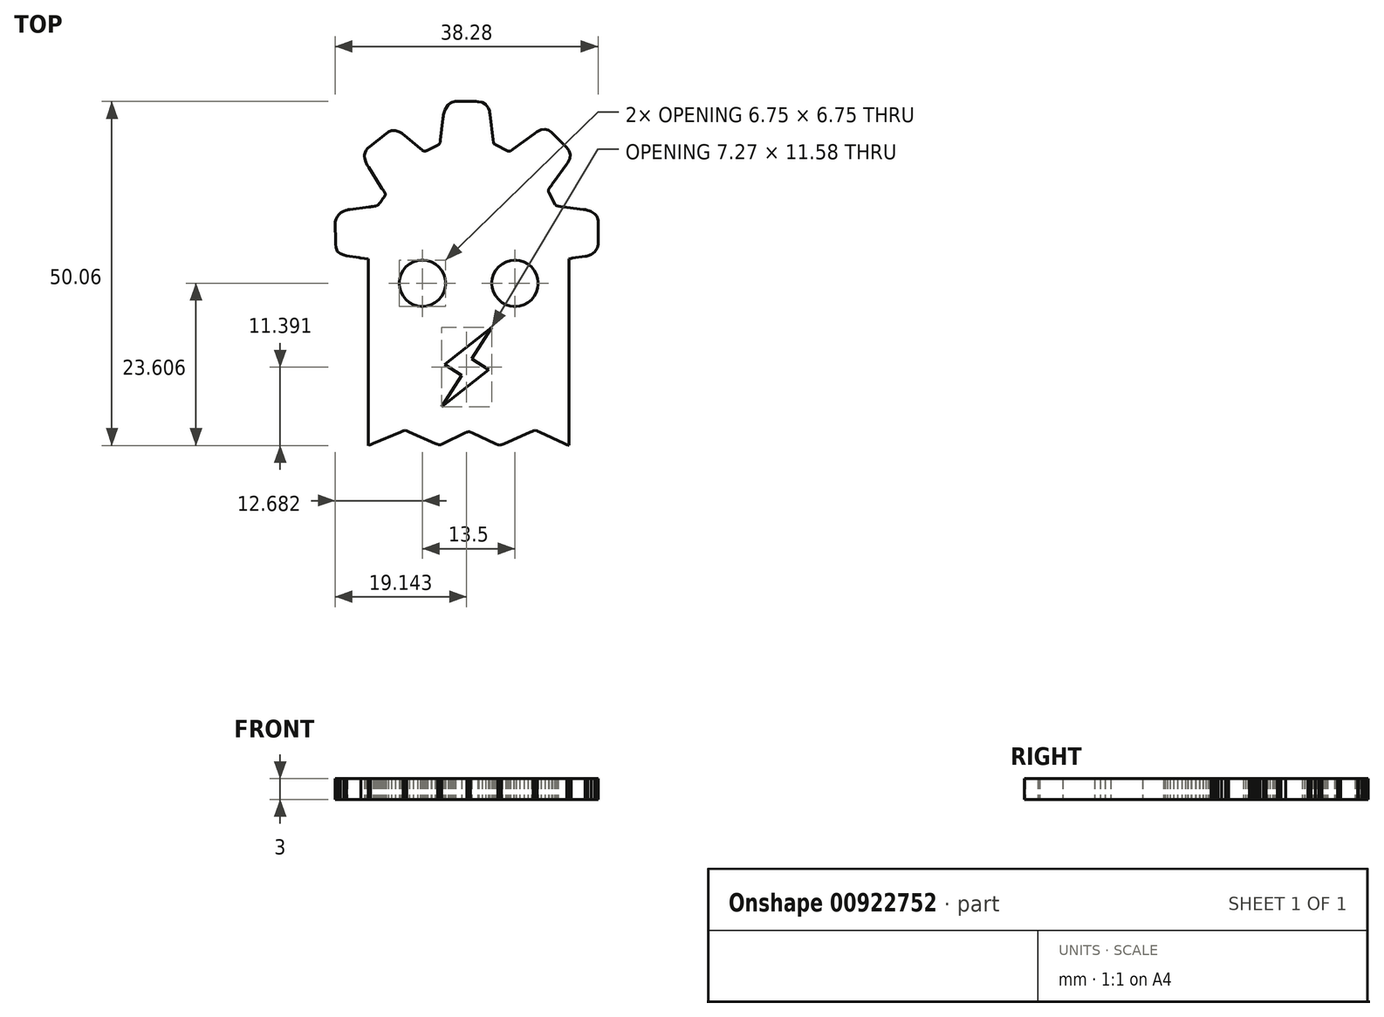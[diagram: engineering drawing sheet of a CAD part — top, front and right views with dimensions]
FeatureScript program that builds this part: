
annotation { "Feature Type Name" : "Feature", "Feature Type Description" : "" }
export const myFeature = defineFeature(function(context is Context, id is Id, definition is map)
    precondition{}
    {
        {
            var Q0;
            Q0=qCreatedBy(makeId("Top.planeOp"),FACE);
            var sketch = newSketch(context, id + "F0", { "sketchPlane" : qUnion([Q0])});
            skLineSegment(sketch, "E0", {"start": v(2.48, 0.36) * mm, "end": v(2.48, -4.17) * mm});
            skLineSegment(sketch, "E1", {"start": v(2.48, -4.17) * mm, "end": v(2.48, -4.17) * mm});
            skLineSegment(sketch, "E2", {"start": v(2.48, -4.17) * mm, "end": v(2.44, -4.15) * mm});
            skLineSegment(sketch, "E3", {"start": v(2.44, -4.15) * mm, "end": v(2.43, -4.15) * mm});
            skLineSegment(sketch, "E4", {"start": v(2.43, -4.15) * mm, "end": v(2.37, -4.12) * mm});
            skLineSegment(sketch, "E5", {"start": v(2.37, -4.12) * mm, "end": v(1.78, -3.85) * mm});
            skLineSegment(sketch, "E6", {"start": v(1.78, -3.85) * mm, "end": v(1.72, -3.82) * mm});
            skLineSegment(sketch, "E7", {"start": v(1.72, -3.82) * mm, "end": v(1.7, -3.82) * mm});
            skLineSegment(sketch, "E8", {"start": v(1.7, -3.82) * mm, "end": v(1.66, -3.8) * mm});
            skLineSegment(sketch, "E9", {"start": v(1.66, -3.8) * mm, "end": v(1.62, -3.82) * mm});
            skLineSegment(sketch, "E10", {"start": v(1.62, -3.82) * mm, "end": v(1.6, -3.82) * mm});
            skLineSegment(sketch, "E11", {"start": v(1.6, -3.82) * mm, "end": v(1.54, -3.85) * mm});
            skLineSegment(sketch, "E12", {"start": v(1.54, -3.85) * mm, "end": v(0.9, -4.13) * mm});
            skLineSegment(sketch, "E13", {"start": v(0.9, -4.13) * mm, "end": v(0.84, -4.16) * mm});
            skLineSegment(sketch, "E14", {"start": v(0.84, -4.16) * mm, "end": v(0.83, -4.16) * mm});
            skLineSegment(sketch, "E15", {"start": v(0.83, -4.16) * mm, "end": v(0.8, -4.16) * mm});
            skLineSegment(sketch, "E16", {"start": v(0.8, -4.16) * mm, "end": v(0.77, -4.16) * mm});
            skLineSegment(sketch, "E17", {"start": v(0.77, -4.16) * mm, "end": v(0.76, -4.16) * mm});
            skLineSegment(sketch, "E18", {"start": v(0.76, -4.16) * mm, "end": v(0.7, -4.13) * mm});
            skLineSegment(sketch, "E19", {"start": v(0.7, -4.13) * mm, "end": v(0.15, -3.87) * mm});
            skLineSegment(sketch, "E20", {"start": v(0.15, -3.87) * mm, "end": v(0.1, -3.85) * mm});
            skLineSegment(sketch, "E21", {"start": v(0.1, -3.85) * mm, "end": v(0.09, -3.84) * mm});
            skLineSegment(sketch, "E22", {"start": v(0.09, -3.84) * mm, "end": v(0.05, -3.84) * mm});
            skLineSegment(sketch, "E23", {"start": v(0.05, -3.84) * mm, "end": v(0.01, -3.84) * mm});
            skLineSegment(sketch, "E24", {"start": v(0.01, -3.84) * mm, "end": v(0, -3.85) * mm});
            skLineSegment(sketch, "E25", {"start": v(0, -3.85) * mm, "end": v(-0.05, -3.87) * mm});
            skLineSegment(sketch, "E26", {"start": v(-0.05, -3.87) * mm, "end": v(-0.56, -4.12) * mm});
            skLineSegment(sketch, "E27", {"start": v(-0.56, -4.12) * mm, "end": v(-0.61, -4.15) * mm});
            skLineSegment(sketch, "E28", {"start": v(-0.61, -4.15) * mm, "end": v(-0.62, -4.15) * mm});
            skLineSegment(sketch, "E29", {"start": v(-0.62, -4.15) * mm, "end": v(-0.66, -4.16) * mm});
            skLineSegment(sketch, "E30", {"start": v(-0.66, -4.16) * mm, "end": v(-0.7, -4.15) * mm});
            skLineSegment(sketch, "E31", {"start": v(-0.7, -4.15) * mm, "end": v(-0.7, -4.15) * mm});
            skLineSegment(sketch, "E32", {"start": v(-0.7, -4.15) * mm, "end": v(-0.77, -4.12) * mm});
            skLineSegment(sketch, "E33", {"start": v(-0.77, -4.12) * mm, "end": v(-1.39, -3.84) * mm});
            skLineSegment(sketch, "E34", {"start": v(-1.39, -3.84) * mm, "end": v(-1.45, -3.81) * mm});
            skLineSegment(sketch, "E35", {"start": v(-1.45, -3.81) * mm, "end": v(-1.46, -3.81) * mm});
            skLineSegment(sketch, "E36", {"start": v(-1.46, -3.81) * mm, "end": v(-1.5, -3.8) * mm});
            skLineSegment(sketch, "E37", {"start": v(-1.5, -3.8) * mm, "end": v(-1.53, -3.81) * mm});
            skLineSegment(sketch, "E38", {"start": v(-1.53, -3.81) * mm, "end": v(-1.54, -3.81) * mm});
            skLineSegment(sketch, "E39", {"start": v(-1.54, -3.81) * mm, "end": v(-1.6, -3.84) * mm});
            skLineSegment(sketch, "E40", {"start": v(-1.6, -3.84) * mm, "end": v(-2.27, -4.12) * mm});
            skLineSegment(sketch, "E41", {"start": v(-2.27, -4.12) * mm, "end": v(-2.33, -4.15) * mm});
            skLineSegment(sketch, "E42", {"start": v(-2.33, -4.15) * mm, "end": v(-2.34, -4.15) * mm});
            skLineSegment(sketch, "E43", {"start": v(-2.34, -4.15) * mm, "end": v(-2.38, -4.17) * mm});
            skLineSegment(sketch, "E44", {"start": v(-2.38, -4.17) * mm, "end": v(-2.38, -4.17) * mm});
            skLineSegment(sketch, "E45", {"start": v(-2.38, -4.17) * mm, "end": v(-2.38, 0.35) * mm});
            skLineSegment(sketch, "E46", {"start": v(-2.38, 0.35) * mm, "end": v(-2.4, 0.35) * mm});
            skLineSegment(sketch, "E47", {"start": v(-2.4, 0.35) * mm, "end": v(-2.56, 0.37) * mm});
            skLineSegment(sketch, "E48", {"start": v(-2.56, 0.37) * mm, "end": v(-2.58, 0.38) * mm});
            skLineSegment(sketch, "E49", {"start": v(-2.58, 0.38) * mm, "end": v(-2.6, 0.38) * mm});
            skLineSegment(sketch, "E50", {"start": v(-2.6, 0.38) * mm, "end": v(-2.92, 0.43) * mm});
            skLineSegment(sketch, "E51", {"start": v(-2.92, 0.43) * mm, "end": v(-2.95, 0.44) * mm});
            skLineSegment(sketch, "E52", {"start": v(-2.95, 0.44) * mm, "end": v(-2.98, 0.45) * mm});
            skLineSegment(sketch, "E53", {"start": v(-2.98, 0.45) * mm, "end": v(-3.06, 0.48) * mm});
            skLineSegment(sketch, "E54", {"start": v(-3.06, 0.48) * mm, "end": v(-3.13, 0.54) * mm});
            skLineSegment(sketch, "E55", {"start": v(-3.13, 0.54) * mm, "end": v(-3.17, 0.62) * mm});
            skLineSegment(sketch, "E56", {"start": v(-3.17, 0.62) * mm, "end": v(-3.18, 0.71) * mm});
            skLineSegment(sketch, "E57", {"start": v(-3.18, 0.71) * mm, "end": v(-3.18, 0.74) * mm});
            skLineSegment(sketch, "E58", {"start": v(-3.18, 0.74) * mm, "end": v(-3.18, 0.85) * mm});
            skLineSegment(sketch, "E59", {"start": v(-3.18, 0.85) * mm, "end": v(-3.19, 1.14) * mm});
            skLineSegment(sketch, "E60", {"start": v(-3.19, 1.14) * mm, "end": v(-3.19, 1.17) * mm});
            skLineSegment(sketch, "E61", {"start": v(-3.19, 1.17) * mm, "end": v(-3.19, 1.2) * mm});
            skLineSegment(sketch, "E62", {"start": v(-3.19, 1.2) * mm, "end": v(-3.19, 1.25) * mm});
            skLineSegment(sketch, "E63", {"start": v(-3.19, 1.25) * mm, "end": v(-3.17, 1.32) * mm});
            skLineSegment(sketch, "E64", {"start": v(-3.17, 1.32) * mm, "end": v(-3.14, 1.38) * mm});
            skLineSegment(sketch, "E65", {"start": v(-3.14, 1.38) * mm, "end": v(-3.1, 1.43) * mm});
            skLineSegment(sketch, "E66", {"start": v(-3.1, 1.43) * mm, "end": v(-3.05, 1.47) * mm});
            skLineSegment(sketch, "E67", {"start": v(-3.05, 1.47) * mm, "end": v(-3, 1.5) * mm});
            skLineSegment(sketch, "E68", {"start": v(-3, 1.5) * mm, "end": v(-2.94, 1.53) * mm});
            skLineSegment(sketch, "E69", {"start": v(-2.94, 1.53) * mm, "end": v(-2.9, 1.54) * mm});
            skLineSegment(sketch, "E70", {"start": v(-2.9, 1.54) * mm, "end": v(-2.88, 1.55) * mm});
            skLineSegment(sketch, "E71", {"start": v(-2.88, 1.55) * mm, "end": v(-2.83, 1.55) * mm});
            skLineSegment(sketch, "E72", {"start": v(-2.83, 1.55) * mm, "end": v(-2.37, 1.61) * mm});
            skLineSegment(sketch, "E73", {"start": v(-2.37, 1.61) * mm, "end": v(-2.33, 1.62) * mm});
            skLineSegment(sketch, "E74", {"start": v(-2.33, 1.62) * mm, "end": v(-2.31, 1.62) * mm});
            skLineSegment(sketch, "E75", {"start": v(-2.31, 1.62) * mm, "end": v(-2.27, 1.62) * mm});
            skLineSegment(sketch, "E76", {"start": v(-2.27, 1.62) * mm, "end": v(-2.23, 1.63) * mm});
            skLineSegment(sketch, "E77", {"start": v(-2.23, 1.63) * mm, "end": v(-2.2, 1.64) * mm});
            skLineSegment(sketch, "E78", {"start": v(-2.2, 1.64) * mm, "end": v(-2.17, 1.65) * mm});
            skLineSegment(sketch, "E79", {"start": v(-2.17, 1.65) * mm, "end": v(-2.14, 1.67) * mm});
            skLineSegment(sketch, "E80", {"start": v(-2.14, 1.67) * mm, "end": v(-2.12, 1.7) * mm});
            skLineSegment(sketch, "E81", {"start": v(-2.12, 1.7) * mm, "end": v(-2.1, 1.73) * mm});
            skLineSegment(sketch, "E82", {"start": v(-2.1, 1.73) * mm, "end": v(-2.07, 1.76) * mm});
            skLineSegment(sketch, "E83", {"start": v(-2.07, 1.76) * mm, "end": v(-2.06, 1.78) * mm});
            skLineSegment(sketch, "E84", {"start": v(-2.06, 1.78) * mm, "end": v(-2.06, 1.79) * mm});
            skLineSegment(sketch, "E85", {"start": v(-2.06, 1.79) * mm, "end": v(-2.03, 1.81) * mm});
            skLineSegment(sketch, "E86", {"start": v(-2.03, 1.81) * mm, "end": v(-2, 1.85) * mm});
            skLineSegment(sketch, "E87", {"start": v(-2, 1.85) * mm, "end": v(-1.98, 1.88) * mm});
            skLineSegment(sketch, "E88", {"start": v(-1.98, 1.88) * mm, "end": v(-1.97, 1.91) * mm});
            skLineSegment(sketch, "E89", {"start": v(-1.97, 1.91) * mm, "end": v(-1.97, 1.92) * mm});
            skLineSegment(sketch, "E90", {"start": v(-1.97, 1.92) * mm, "end": v(-1.97, 1.93) * mm});
            skLineSegment(sketch, "E91", {"start": v(-1.97, 1.93) * mm, "end": v(-1.98, 1.95) * mm});
            skLineSegment(sketch, "E92", {"start": v(-1.98, 1.95) * mm, "end": v(-2, 1.99) * mm});
            skLineSegment(sketch, "E93", {"start": v(-2, 1.99) * mm, "end": v(-2.03, 2.03) * mm});
            skLineSegment(sketch, "E94", {"start": v(-2.03, 2.03) * mm, "end": v(-2.05, 2.05) * mm});
            skLineSegment(sketch, "E95", {"start": v(-2.05, 2.05) * mm, "end": v(-2.05, 2.06) * mm});
            skLineSegment(sketch, "E96", {"start": v(-2.05, 2.06) * mm, "end": v(-2.08, 2.1) * mm});
            skLineSegment(sketch, "E97", {"start": v(-2.08, 2.1) * mm, "end": v(-2.38, 2.57) * mm});
            skLineSegment(sketch, "E98", {"start": v(-2.38, 2.57) * mm, "end": v(-2.4, 2.62) * mm});
            skLineSegment(sketch, "E99", {"start": v(-2.4, 2.62) * mm, "end": v(-2.42, 2.63) * mm});
            skLineSegment(sketch, "E100", {"start": v(-2.42, 2.63) * mm, "end": v(-2.45, 2.71) * mm});
            skLineSegment(sketch, "E101", {"start": v(-2.45, 2.71) * mm, "end": v(-2.47, 2.8) * mm});
            skLineSegment(sketch, "E102", {"start": v(-2.47, 2.8) * mm, "end": v(-2.47, 2.8) * mm});
            skLineSegment(sketch, "E103", {"start": v(-2.47, 2.8) * mm, "end": v(-2.48, 2.82) * mm});
            skLineSegment(sketch, "E104", {"start": v(-2.48, 2.82) * mm, "end": v(-2.48, 2.87) * mm});
            skLineSegment(sketch, "E105", {"start": v(-2.48, 2.87) * mm, "end": v(-2.46, 2.93) * mm});
            skLineSegment(sketch, "E106", {"start": v(-2.46, 2.93) * mm, "end": v(-2.44, 3) * mm});
            skLineSegment(sketch, "E107", {"start": v(-2.44, 3) * mm, "end": v(-2.4, 3.03) * mm});
            skLineSegment(sketch, "E108", {"start": v(-2.4, 3.03) * mm, "end": v(-2.4, 3.04) * mm});
            skLineSegment(sketch, "E109", {"start": v(-2.4, 3.04) * mm, "end": v(-2.35, 3.07) * mm});
            skLineSegment(sketch, "E110", {"start": v(-2.35, 3.07) * mm, "end": v(-1.95, 3.4) * mm});
            skLineSegment(sketch, "E111", {"start": v(-1.95, 3.4) * mm, "end": v(-1.91, 3.42) * mm});
            skLineSegment(sketch, "E112", {"start": v(-1.91, 3.42) * mm, "end": v(-1.9, 3.43) * mm});
            skLineSegment(sketch, "E113", {"start": v(-1.9, 3.43) * mm, "end": v(-1.83, 3.46) * mm});
            skLineSegment(sketch, "E114", {"start": v(-1.83, 3.46) * mm, "end": v(-1.73, 3.47) * mm});
            skLineSegment(sketch, "E115", {"start": v(-1.73, 3.47) * mm, "end": v(-1.64, 3.44) * mm});
            skLineSegment(sketch, "E116", {"start": v(-1.64, 3.44) * mm, "end": v(-1.57, 3.4) * mm});
            skLineSegment(sketch, "E117", {"start": v(-1.57, 3.4) * mm, "end": v(-1.55, 3.38) * mm});
            skLineSegment(sketch, "E118", {"start": v(-1.55, 3.38) * mm, "end": v(-1.5, 3.35) * mm});
            skLineSegment(sketch, "E119", {"start": v(-1.5, 3.35) * mm, "end": v(-1.12, 3.03) * mm});
            skLineSegment(sketch, "E120", {"start": v(-1.12, 3.03) * mm, "end": v(-1.09, 3) * mm});
            skLineSegment(sketch, "E121", {"start": v(-1.09, 3) * mm, "end": v(-1.08, 2.99) * mm});
            skLineSegment(sketch, "E122", {"start": v(-1.08, 2.99) * mm, "end": v(-1.06, 2.97) * mm});
            skLineSegment(sketch, "E123", {"start": v(-1.06, 2.97) * mm, "end": v(-1.03, 2.97) * mm});
            skLineSegment(sketch, "E124", {"start": v(-1.03, 2.97) * mm, "end": v(-1, 2.97) * mm});
            skLineSegment(sketch, "E125", {"start": v(-1, 2.97) * mm, "end": v(-0.98, 2.98) * mm});
            skLineSegment(sketch, "E126", {"start": v(-0.98, 2.98) * mm, "end": v(-0.97, 2.98) * mm});
            skLineSegment(sketch, "E127", {"start": v(-0.97, 2.98) * mm, "end": v(-0.95, 3) * mm});
            skLineSegment(sketch, "E128", {"start": v(-0.95, 3) * mm, "end": v(-0.71, 3.1) * mm});
            skLineSegment(sketch, "E129", {"start": v(-0.71, 3.1) * mm, "end": v(-0.69, 3.12) * mm});
            skLineSegment(sketch, "E130", {"start": v(-0.69, 3.12) * mm, "end": v(-0.68, 3.12) * mm});
            skLineSegment(sketch, "E131", {"start": v(-0.68, 3.12) * mm, "end": v(-0.66, 3.14) * mm});
            skLineSegment(sketch, "E132", {"start": v(-0.66, 3.14) * mm, "end": v(-0.64, 3.18) * mm});
            skLineSegment(sketch, "E133", {"start": v(-0.64, 3.18) * mm, "end": v(-0.64, 3.18) * mm});
            skLineSegment(sketch, "E134", {"start": v(-0.64, 3.18) * mm, "end": v(-0.64, 3.24) * mm});
            skLineSegment(sketch, "E135", {"start": v(-0.64, 3.24) * mm, "end": v(-0.57, 3.77) * mm});
            skLineSegment(sketch, "E136", {"start": v(-0.57, 3.77) * mm, "end": v(-0.57, 3.82) * mm});
            skLineSegment(sketch, "E137", {"start": v(-0.57, 3.82) * mm, "end": v(-0.56, 3.85) * mm});
            skLineSegment(sketch, "E138", {"start": v(-0.56, 3.85) * mm, "end": v(-0.52, 3.98) * mm});
            skLineSegment(sketch, "E139", {"start": v(-0.52, 3.98) * mm, "end": v(-0.44, 4.09) * mm});
            skLineSegment(sketch, "E140", {"start": v(-0.44, 4.09) * mm, "end": v(-0.42, 4.1) * mm});
            skLineSegment(sketch, "E141", {"start": v(-0.42, 4.1) * mm, "end": v(-0.42, 4.11) * mm});
            skLineSegment(sketch, "E142", {"start": v(-0.42, 4.11) * mm, "end": v(-0.4, 4.14) * mm});
            skLineSegment(sketch, "E143", {"start": v(-0.4, 4.14) * mm, "end": v(-0.35, 4.16) * mm});
            skLineSegment(sketch, "E144", {"start": v(-0.35, 4.16) * mm, "end": v(-0.31, 4.17) * mm});
            skLineSegment(sketch, "E145", {"start": v(-0.31, 4.17) * mm, "end": v(-0.28, 4.17) * mm});
            skLineSegment(sketch, "E146", {"start": v(-0.28, 4.17) * mm, "end": v(-0.27, 4.17) * mm});
            skLineSegment(sketch, "E147", {"start": v(-0.27, 4.17) * mm, "end": v(-0.22, 4.17) * mm});
            skLineSegment(sketch, "E148", {"start": v(-0.22, 4.17) * mm, "end": v(0.23, 4.17) * mm});
            skLineSegment(sketch, "E149", {"start": v(0.23, 4.17) * mm, "end": v(0.27, 4.17) * mm});
            skLineSegment(sketch, "E150", {"start": v(0.27, 4.17) * mm, "end": v(0.3, 4.17) * mm});
            skLineSegment(sketch, "E151", {"start": v(0.3, 4.17) * mm, "end": v(0.38, 4.15) * mm});
            skLineSegment(sketch, "E152", {"start": v(0.38, 4.15) * mm, "end": v(0.46, 4.1) * mm});
            skLineSegment(sketch, "E153", {"start": v(0.46, 4.1) * mm, "end": v(0.53, 4.02) * mm});
            skLineSegment(sketch, "E154", {"start": v(0.53, 4.02) * mm, "end": v(0.56, 3.94) * mm});
            skLineSegment(sketch, "E155", {"start": v(0.56, 3.94) * mm, "end": v(0.56, 3.91) * mm});
            skLineSegment(sketch, "E156", {"start": v(0.56, 3.91) * mm, "end": v(0.57, 3.85) * mm});
            skLineSegment(sketch, "E157", {"start": v(0.57, 3.85) * mm, "end": v(0.65, 3.24) * mm});
            skLineSegment(sketch, "E158", {"start": v(0.65, 3.24) * mm, "end": v(0.65, 3.18) * mm});
            skLineSegment(sketch, "E159", {"start": v(0.65, 3.18) * mm, "end": v(0.65, 3.18) * mm});
            skLineSegment(sketch, "E160", {"start": v(0.65, 3.18) * mm, "end": v(0.67, 3.15) * mm});
            skLineSegment(sketch, "E161", {"start": v(0.67, 3.15) * mm, "end": v(0.69, 3.13) * mm});
            skLineSegment(sketch, "E162", {"start": v(0.69, 3.13) * mm, "end": v(0.7, 3.13) * mm});
            skLineSegment(sketch, "E163", {"start": v(0.7, 3.13) * mm, "end": v(0.72, 3.11) * mm});
            skLineSegment(sketch, "E164", {"start": v(0.72, 3.11) * mm, "end": v(0.97, 2.98) * mm});
            skLineSegment(sketch, "E165", {"start": v(0.97, 2.98) * mm, "end": v(1, 2.97) * mm});
            skLineSegment(sketch, "E166", {"start": v(1, 2.97) * mm, "end": v(1, 2.97) * mm});
            skLineSegment(sketch, "E167", {"start": v(1, 2.97) * mm, "end": v(1.03, 2.96) * mm});
            skLineSegment(sketch, "E168", {"start": v(1.03, 2.96) * mm, "end": v(1.06, 2.97) * mm});
            skLineSegment(sketch, "E169", {"start": v(1.06, 2.97) * mm, "end": v(1.06, 2.97) * mm});
            skLineSegment(sketch, "E170", {"start": v(1.06, 2.97) * mm, "end": v(1.11, 3.01) * mm});
            skLineSegment(sketch, "E171", {"start": v(1.11, 3.01) * mm, "end": v(1.65, 3.4) * mm});
            skLineSegment(sketch, "E172", {"start": v(1.65, 3.4) * mm, "end": v(1.7, 3.43) * mm});
            skLineSegment(sketch, "E173", {"start": v(1.7, 3.43) * mm, "end": v(1.73, 3.45) * mm});
            skLineSegment(sketch, "E174", {"start": v(1.73, 3.45) * mm, "end": v(1.8, 3.49) * mm});
            skLineSegment(sketch, "E175", {"start": v(1.8, 3.49) * mm, "end": v(1.9, 3.5) * mm});
            skLineSegment(sketch, "E176", {"start": v(1.9, 3.5) * mm, "end": v(1.99, 3.47) * mm});
            skLineSegment(sketch, "E177", {"start": v(1.99, 3.47) * mm, "end": v(2.06, 3.43) * mm});
            skLineSegment(sketch, "E178", {"start": v(2.06, 3.43) * mm, "end": v(2.08, 3.4) * mm});
            skLineSegment(sketch, "E179", {"start": v(2.08, 3.4) * mm, "end": v(2.1, 3.38) * mm});
            skLineSegment(sketch, "E180", {"start": v(2.1, 3.38) * mm, "end": v(2.39, 3.1) * mm});
            skLineSegment(sketch, "E181", {"start": v(2.39, 3.1) * mm, "end": v(2.42, 3.07) * mm});
            skLineSegment(sketch, "E182", {"start": v(2.42, 3.07) * mm, "end": v(2.44, 3.05) * mm});
            skLineSegment(sketch, "E183", {"start": v(2.44, 3.05) * mm, "end": v(2.49, 2.98) * mm});
            skLineSegment(sketch, "E184", {"start": v(2.49, 2.98) * mm, "end": v(2.52, 2.88) * mm});
            skLineSegment(sketch, "E185", {"start": v(2.52, 2.88) * mm, "end": v(2.5, 2.78) * mm});
            skLineSegment(sketch, "E186", {"start": v(2.5, 2.78) * mm, "end": v(2.47, 2.7) * mm});
            skLineSegment(sketch, "E187", {"start": v(2.47, 2.7) * mm, "end": v(2.45, 2.68) * mm});
            skLineSegment(sketch, "E188", {"start": v(2.45, 2.68) * mm, "end": v(2.42, 2.64) * mm});
            skLineSegment(sketch, "E189", {"start": v(2.42, 2.64) * mm, "end": v(2.12, 2.22) * mm});
            skLineSegment(sketch, "E190", {"start": v(2.12, 2.22) * mm, "end": v(2.09, 2.18) * mm});
            skLineSegment(sketch, "E191", {"start": v(2.09, 2.18) * mm, "end": v(2.08, 2.17) * mm});
            skLineSegment(sketch, "E192", {"start": v(2.08, 2.17) * mm, "end": v(2, 2.05) * mm});
            skLineSegment(sketch, "E193", {"start": v(2, 2.05) * mm, "end": v(2, 2.04) * mm});
            skLineSegment(sketch, "E194", {"start": v(2, 2.04) * mm, "end": v(1.99, 2.04) * mm});
            skLineSegment(sketch, "E195", {"start": v(1.99, 2.04) * mm, "end": v(1.98, 2.02) * mm});
            skLineSegment(sketch, "E196", {"start": v(1.98, 2.02) * mm, "end": v(1.99, 2) * mm});
            skLineSegment(sketch, "E197", {"start": v(1.99, 2) * mm, "end": v(1.99, 1.99) * mm});
            skLineSegment(sketch, "E198", {"start": v(1.99, 1.99) * mm, "end": v(2, 1.96) * mm});
            skLineSegment(sketch, "E199", {"start": v(2, 1.96) * mm, "end": v(2.13, 1.7) * mm});
            skLineSegment(sketch, "E200", {"start": v(2.13, 1.7) * mm, "end": v(2.15, 1.67) * mm});
            skLineSegment(sketch, "E201", {"start": v(2.15, 1.67) * mm, "end": v(2.15, 1.66) * mm});
            skLineSegment(sketch, "E202", {"start": v(2.15, 1.66) * mm, "end": v(2.18, 1.64) * mm});
            skLineSegment(sketch, "E203", {"start": v(2.18, 1.64) * mm, "end": v(2.21, 1.63) * mm});
            skLineSegment(sketch, "E204", {"start": v(2.21, 1.63) * mm, "end": v(2.22, 1.63) * mm});
            skLineSegment(sketch, "E205", {"start": v(2.22, 1.63) * mm, "end": v(2.28, 1.62) * mm});
            skLineSegment(sketch, "E206", {"start": v(2.28, 1.62) * mm, "end": v(2.83, 1.55) * mm});
            skLineSegment(sketch, "E207", {"start": v(2.83, 1.55) * mm, "end": v(2.89, 1.55) * mm});
            skLineSegment(sketch, "E208", {"start": v(2.89, 1.55) * mm, "end": v(2.9, 1.54) * mm});
            skLineSegment(sketch, "E209", {"start": v(2.9, 1.54) * mm, "end": v(3.01, 1.5) * mm});
            skLineSegment(sketch, "E210", {"start": v(3.01, 1.5) * mm, "end": v(3.1, 1.44) * mm});
            skLineSegment(sketch, "E211", {"start": v(3.1, 1.44) * mm, "end": v(3.12, 1.43) * mm});
            skLineSegment(sketch, "E212", {"start": v(3.12, 1.43) * mm, "end": v(3.13, 1.42) * mm});
            skLineSegment(sketch, "E213", {"start": v(3.13, 1.42) * mm, "end": v(3.15, 1.4) * mm});
            skLineSegment(sketch, "E214", {"start": v(3.15, 1.4) * mm, "end": v(3.17, 1.36) * mm});
            skLineSegment(sketch, "E215", {"start": v(3.17, 1.36) * mm, "end": v(3.18, 1.32) * mm});
            skLineSegment(sketch, "E216", {"start": v(3.18, 1.32) * mm, "end": v(3.19, 1.29) * mm});
            skLineSegment(sketch, "E217", {"start": v(3.19, 1.29) * mm, "end": v(3.19, 1.28) * mm});
            skLineSegment(sketch, "E218", {"start": v(3.19, 1.28) * mm, "end": v(3.19, 1.23) * mm});
            skLineSegment(sketch, "E219", {"start": v(3.19, 1.23) * mm, "end": v(3.19, 0.78) * mm});
            skLineSegment(sketch, "E220", {"start": v(3.19, 0.78) * mm, "end": v(3.19, 0.73) * mm});
            skLineSegment(sketch, "E221", {"start": v(3.19, 0.73) * mm, "end": v(3.19, 0.7) * mm});
            skLineSegment(sketch, "E222", {"start": v(3.19, 0.7) * mm, "end": v(3.17, 0.61) * mm});
            skLineSegment(sketch, "E223", {"start": v(3.17, 0.61) * mm, "end": v(3.11, 0.52) * mm});
            skLineSegment(sketch, "E224", {"start": v(3.11, 0.52) * mm, "end": v(3.02, 0.46) * mm});
            skLineSegment(sketch, "E225", {"start": v(3.02, 0.46) * mm, "end": v(2.94, 0.42) * mm});
            skLineSegment(sketch, "E226", {"start": v(2.94, 0.42) * mm, "end": v(2.9, 0.42) * mm});
            skLineSegment(sketch, "E227", {"start": v(2.9, 0.42) * mm, "end": v(2.88, 0.41) * mm});
            skLineSegment(sketch, "E228", {"start": v(2.88, 0.41) * mm, "end": v(2.57, 0.37) * mm});
            skLineSegment(sketch, "E229", {"start": v(2.57, 0.37) * mm, "end": v(2.54, 0.37) * mm});
            skLineSegment(sketch, "E230", {"start": v(2.54, 0.37) * mm, "end": v(2.53, 0.37) * mm});
            skLineSegment(sketch, "E231", {"start": v(2.53, 0.37) * mm, "end": v(2.49, 0.36) * mm});
            skLineSegment(sketch, "E232", {"start": v(2.49, 0.36) * mm, "end": v(2.48, 0.36) * mm});
            skLineSegment(sketch, "E233", {"start": v(0.6, -1.3) * mm, "end": v(0.6, -1.3) * mm});
            skLineSegment(sketch, "E234", {"start": v(0.6, -1.3) * mm, "end": v(-0.54, -2.21) * mm});
            skLineSegment(sketch, "E235", {"start": v(-0.54, -2.21) * mm, "end": v(-0.12, -2.47) * mm});
            skLineSegment(sketch, "E236", {"start": v(-0.12, -2.47) * mm, "end": v(-0.6, -3.24) * mm});
            skLineSegment(sketch, "E237", {"start": v(-0.6, -3.24) * mm, "end": v(-0.6, -3.24) * mm});
            skLineSegment(sketch, "E238", {"start": v(-0.6, -3.24) * mm, "end": v(0.54, -2.33) * mm});
            skLineSegment(sketch, "E239", {"start": v(0.54, -2.33) * mm, "end": v(0.13, -2.07) * mm});
            skLineSegment(sketch, "E240", {"start": v(0.13, -2.07) * mm, "end": v(0.6, -1.3) * mm});
            skLineSegment(sketch, "E241", {"start": v(-1.07, 0.33) * mm, "end": v(-1.1, 0.33) * mm});
            skLineSegment(sketch, "E242", {"start": v(-1.1, 0.33) * mm, "end": v(-1.19, 0.31) * mm});
            skLineSegment(sketch, "E243", {"start": v(-1.19, 0.31) * mm, "end": v(-1.3, 0.28) * mm});
            skLineSegment(sketch, "E244", {"start": v(-1.3, 0.28) * mm, "end": v(-1.39, 0.23) * mm});
            skLineSegment(sketch, "E245", {"start": v(-1.39, 0.23) * mm, "end": v(-1.47, 0.16) * mm});
            skLineSegment(sketch, "E246", {"start": v(-1.47, 0.16) * mm, "end": v(-1.54, 0.08) * mm});
            skLineSegment(sketch, "E247", {"start": v(-1.54, 0.08) * mm, "end": v(-1.6, -0.02) * mm});
            skLineSegment(sketch, "E248", {"start": v(-1.6, -0.02) * mm, "end": v(-1.63, -0.12) * mm});
            skLineSegment(sketch, "E249", {"start": v(-1.63, -0.12) * mm, "end": v(-1.64, -0.2) * mm});
            skLineSegment(sketch, "E250", {"start": v(-1.64, -0.2) * mm, "end": v(-1.64, -0.24) * mm});
            skLineSegment(sketch, "E251", {"start": v(-1.64, -0.24) * mm, "end": v(-1.64, -0.26) * mm});
            skLineSegment(sketch, "E252", {"start": v(-1.64, -0.26) * mm, "end": v(-1.63, -0.35) * mm});
            skLineSegment(sketch, "E253", {"start": v(-1.63, -0.35) * mm, "end": v(-1.6, -0.45) * mm});
            skLineSegment(sketch, "E254", {"start": v(-1.6, -0.45) * mm, "end": v(-1.54, -0.55) * mm});
            skLineSegment(sketch, "E255", {"start": v(-1.54, -0.55) * mm, "end": v(-1.48, -0.63) * mm});
            skLineSegment(sketch, "E256", {"start": v(-1.48, -0.63) * mm, "end": v(-1.4, -0.7) * mm});
            skLineSegment(sketch, "E257", {"start": v(-1.4, -0.7) * mm, "end": v(-1.3, -0.75) * mm});
            skLineSegment(sketch, "E258", {"start": v(-1.3, -0.75) * mm, "end": v(-1.2, -0.79) * mm});
            skLineSegment(sketch, "E259", {"start": v(-1.2, -0.79) * mm, "end": v(-1.1, -0.8) * mm});
            skLineSegment(sketch, "E260", {"start": v(-1.1, -0.8) * mm, "end": v(-1.08, -0.8) * mm});
            skLineSegment(sketch, "E261", {"start": v(-1.08, -0.8) * mm, "end": v(-1.05, -0.8) * mm});
            skLineSegment(sketch, "E262", {"start": v(-1.05, -0.8) * mm, "end": v(-0.97, -0.79) * mm});
            skLineSegment(sketch, "E263", {"start": v(-0.97, -0.79) * mm, "end": v(-0.86, -0.76) * mm});
            skLineSegment(sketch, "E264", {"start": v(-0.86, -0.76) * mm, "end": v(-0.76, -0.7) * mm});
            skLineSegment(sketch, "E265", {"start": v(-0.76, -0.7) * mm, "end": v(-0.68, -0.64) * mm});
            skLineSegment(sketch, "E266", {"start": v(-0.68, -0.64) * mm, "end": v(-0.61, -0.55) * mm});
            skLineSegment(sketch, "E267", {"start": v(-0.61, -0.55) * mm, "end": v(-0.56, -0.46) * mm});
            skLineSegment(sketch, "E268", {"start": v(-0.56, -0.46) * mm, "end": v(-0.53, -0.35) * mm});
            skLineSegment(sketch, "E269", {"start": v(-0.53, -0.35) * mm, "end": v(-0.51, -0.27) * mm});
            skLineSegment(sketch, "E270", {"start": v(-0.51, -0.27) * mm, "end": v(-0.51, -0.24) * mm});
            skLineSegment(sketch, "E271", {"start": v(-0.51, -0.24) * mm, "end": v(-0.51, -0.21) * mm});
            skLineSegment(sketch, "E272", {"start": v(-0.51, -0.21) * mm, "end": v(-0.52, -0.13) * mm});
            skLineSegment(sketch, "E273", {"start": v(-0.52, -0.13) * mm, "end": v(-0.56, -0.02) * mm});
            skLineSegment(sketch, "E274", {"start": v(-0.56, -0.02) * mm, "end": v(-0.6, 0.08) * mm});
            skLineSegment(sketch, "E275", {"start": v(-0.6, 0.08) * mm, "end": v(-0.68, 0.16) * mm});
            skLineSegment(sketch, "E276", {"start": v(-0.68, 0.16) * mm, "end": v(-0.76, 0.23) * mm});
            skLineSegment(sketch, "E277", {"start": v(-0.76, 0.23) * mm, "end": v(-0.86, 0.28) * mm});
            skLineSegment(sketch, "E278", {"start": v(-0.86, 0.28) * mm, "end": v(-0.96, 0.31) * mm});
            skLineSegment(sketch, "E279", {"start": v(-0.96, 0.31) * mm, "end": v(-1.05, 0.32) * mm});
            skLineSegment(sketch, "E280", {"start": v(-1.05, 0.32) * mm, "end": v(-1.07, 0.33) * mm});
            skLineSegment(sketch, "E281", {"start": v(1.18, 0.33) * mm, "end": v(1.15, 0.33) * mm});
            skLineSegment(sketch, "E282", {"start": v(1.15, 0.33) * mm, "end": v(1.06, 0.31) * mm});
            skLineSegment(sketch, "E283", {"start": v(1.06, 0.31) * mm, "end": v(0.96, 0.28) * mm});
            skLineSegment(sketch, "E284", {"start": v(0.96, 0.28) * mm, "end": v(0.86, 0.23) * mm});
            skLineSegment(sketch, "E285", {"start": v(0.86, 0.23) * mm, "end": v(0.78, 0.16) * mm});
            skLineSegment(sketch, "E286", {"start": v(0.78, 0.16) * mm, "end": v(0.7, 0.08) * mm});
            skLineSegment(sketch, "E287", {"start": v(0.7, 0.08) * mm, "end": v(0.66, -0.02) * mm});
            skLineSegment(sketch, "E288", {"start": v(0.66, -0.02) * mm, "end": v(0.62, -0.12) * mm});
            skLineSegment(sketch, "E289", {"start": v(0.62, -0.12) * mm, "end": v(0.61, -0.2) * mm});
            skLineSegment(sketch, "E290", {"start": v(0.61, -0.2) * mm, "end": v(0.61, -0.24) * mm});
            skLineSegment(sketch, "E291", {"start": v(0.61, -0.24) * mm, "end": v(0.61, -0.26) * mm});
            skLineSegment(sketch, "E292", {"start": v(0.61, -0.26) * mm, "end": v(0.62, -0.35) * mm});
            skLineSegment(sketch, "E293", {"start": v(0.62, -0.35) * mm, "end": v(0.65, -0.45) * mm});
            skLineSegment(sketch, "E294", {"start": v(0.65, -0.45) * mm, "end": v(0.7, -0.55) * mm});
            skLineSegment(sketch, "E295", {"start": v(0.7, -0.55) * mm, "end": v(0.77, -0.63) * mm});
            skLineSegment(sketch, "E296", {"start": v(0.77, -0.63) * mm, "end": v(0.86, -0.7) * mm});
            skLineSegment(sketch, "E297", {"start": v(0.86, -0.7) * mm, "end": v(0.95, -0.75) * mm});
            skLineSegment(sketch, "E298", {"start": v(0.95, -0.75) * mm, "end": v(1.06, -0.79) * mm});
            skLineSegment(sketch, "E299", {"start": v(1.06, -0.79) * mm, "end": v(1.14, -0.8) * mm});
            skLineSegment(sketch, "E300", {"start": v(1.14, -0.8) * mm, "end": v(1.17, -0.8) * mm});
            skLineSegment(sketch, "E301", {"start": v(1.17, -0.8) * mm, "end": v(1.2, -0.8) * mm});
            skLineSegment(sketch, "E302", {"start": v(1.2, -0.8) * mm, "end": v(1.28, -0.79) * mm});
            skLineSegment(sketch, "E303", {"start": v(1.28, -0.79) * mm, "end": v(1.4, -0.76) * mm});
            skLineSegment(sketch, "E304", {"start": v(1.4, -0.76) * mm, "end": v(1.49, -0.7) * mm});
            skLineSegment(sketch, "E305", {"start": v(1.49, -0.7) * mm, "end": v(1.57, -0.64) * mm});
            skLineSegment(sketch, "E306", {"start": v(1.57, -0.64) * mm, "end": v(1.64, -0.55) * mm});
            skLineSegment(sketch, "E307", {"start": v(1.64, -0.55) * mm, "end": v(1.7, -0.46) * mm});
            skLineSegment(sketch, "E308", {"start": v(1.7, -0.46) * mm, "end": v(1.72, -0.35) * mm});
            skLineSegment(sketch, "E309", {"start": v(1.72, -0.35) * mm, "end": v(1.74, -0.27) * mm});
            skLineSegment(sketch, "E310", {"start": v(1.74, -0.27) * mm, "end": v(1.74, -0.24) * mm});
            skLineSegment(sketch, "E311", {"start": v(1.74, -0.24) * mm, "end": v(1.74, -0.21) * mm});
            skLineSegment(sketch, "E312", {"start": v(1.74, -0.21) * mm, "end": v(1.73, -0.13) * mm});
            skLineSegment(sketch, "E313", {"start": v(1.73, -0.13) * mm, "end": v(1.7, -0.02) * mm});
            skLineSegment(sketch, "E314", {"start": v(1.7, -0.02) * mm, "end": v(1.64, 0.08) * mm});
            skLineSegment(sketch, "E315", {"start": v(1.64, 0.08) * mm, "end": v(1.57, 0.16) * mm});
            skLineSegment(sketch, "E316", {"start": v(1.57, 0.16) * mm, "end": v(1.49, 0.23) * mm});
            skLineSegment(sketch, "E317", {"start": v(1.49, 0.23) * mm, "end": v(1.4, 0.28) * mm});
            skLineSegment(sketch, "E318", {"start": v(1.4, 0.28) * mm, "end": v(1.29, 0.31) * mm});
            skLineSegment(sketch, "E319", {"start": v(1.29, 0.31) * mm, "end": v(1.2, 0.32) * mm});
            skLineSegment(sketch, "E320", {"start": v(1.2, 0.32) * mm, "end": v(1.18, 0.33) * mm});
            skLineSegment(sketch, "E321", {"start": v(1.18, 0.33) * mm, "end": v(1.18, 0.33) * mm});
            skSolve(sketch);
        }
        {
            var Q0;
            Q0=makeQuery(id+"F0.imprint","IMPRINT",FACE,{"disambiguationData":[TD([[makeQuery(id+"F0.imprint","IMPRINT",EDGE,{"derivedFrom":sQuery(id+"F0.wireOp",EDGE,"E0")}),-1.0]])]});
            extrude(context, id + "F1", {"entities" : qUnion([Q0]), "depth" : .25 * mm, "offsetDistance" : 25 * mm});
        }
        {
            var Q0;
            Q0=makeQuery(id+"F1.opExtrude","SWEPT_BODY",BODY,{"disambiguationData":[OSD([sQuery(id+"F0.wireOp",EDGE,"E0"),sQuery(id+"F0.wireOp",EDGE,"E1"),sQuery(id+"F0.wireOp",EDGE,"E2"),sQuery(id+"F0.wireOp",EDGE,"E3"),sQuery(id+"F0.wireOp",EDGE,"E4"),sQuery(id+"F0.wireOp",EDGE,"E5"),sQuery(id+"F0.wireOp",EDGE,"E6"),sQuery(id+"F0.wireOp",EDGE,"E7"),sQuery(id+"F0.wireOp",EDGE,"E8"),sQuery(id+"F0.wireOp",EDGE,"E9"),sQuery(id+"F0.wireOp",EDGE,"E10"),sQuery(id+"F0.wireOp",EDGE,"E11"),sQuery(id+"F0.wireOp",EDGE,"E12"),sQuery(id+"F0.wireOp",EDGE,"E13"),sQuery(id+"F0.wireOp",EDGE,"E14"),sQuery(id+"F0.wireOp",EDGE,"E15"),sQuery(id+"F0.wireOp",EDGE,"E16"),sQuery(id+"F0.wireOp",EDGE,"E17"),sQuery(id+"F0.wireOp",EDGE,"E18"),sQuery(id+"F0.wireOp",EDGE,"E19"),sQuery(id+"F0.wireOp",EDGE,"E20"),sQuery(id+"F0.wireOp",EDGE,"E21"),sQuery(id+"F0.wireOp",EDGE,"E22"),sQuery(id+"F0.wireOp",EDGE,"E23"),sQuery(id+"F0.wireOp",EDGE,"E24"),sQuery(id+"F0.wireOp",EDGE,"E25"),sQuery(id+"F0.wireOp",EDGE,"E26"),sQuery(id+"F0.wireOp",EDGE,"E27"),sQuery(id+"F0.wireOp",EDGE,"E28"),sQuery(id+"F0.wireOp",EDGE,"E29"),sQuery(id+"F0.wireOp",EDGE,"E30"),sQuery(id+"F0.wireOp",EDGE,"E31"),sQuery(id+"F0.wireOp",EDGE,"E32"),sQuery(id+"F0.wireOp",EDGE,"E33"),sQuery(id+"F0.wireOp",EDGE,"E34"),sQuery(id+"F0.wireOp",EDGE,"E35"),sQuery(id+"F0.wireOp",EDGE,"E36"),sQuery(id+"F0.wireOp",EDGE,"E37"),sQuery(id+"F0.wireOp",EDGE,"E38"),sQuery(id+"F0.wireOp",EDGE,"E39"),sQuery(id+"F0.wireOp",EDGE,"E40"),sQuery(id+"F0.wireOp",EDGE,"E41"),sQuery(id+"F0.wireOp",EDGE,"E42"),sQuery(id+"F0.wireOp",EDGE,"E43"),sQuery(id+"F0.wireOp",EDGE,"E44"),sQuery(id+"F0.wireOp",EDGE,"E45"),sQuery(id+"F0.wireOp",EDGE,"E46"),sQuery(id+"F0.wireOp",EDGE,"E47"),sQuery(id+"F0.wireOp",EDGE,"E48"),sQuery(id+"F0.wireOp",EDGE,"E49"),sQuery(id+"F0.wireOp",EDGE,"E50"),sQuery(id+"F0.wireOp",EDGE,"E51"),sQuery(id+"F0.wireOp",EDGE,"E52"),sQuery(id+"F0.wireOp",EDGE,"E53"),sQuery(id+"F0.wireOp",EDGE,"E54"),sQuery(id+"F0.wireOp",EDGE,"E55"),sQuery(id+"F0.wireOp",EDGE,"E56"),sQuery(id+"F0.wireOp",EDGE,"E57"),sQuery(id+"F0.wireOp",EDGE,"E58"),sQuery(id+"F0.wireOp",EDGE,"E59"),sQuery(id+"F0.wireOp",EDGE,"E60"),sQuery(id+"F0.wireOp",EDGE,"E61"),sQuery(id+"F0.wireOp",EDGE,"E62"),sQuery(id+"F0.wireOp",EDGE,"E63"),sQuery(id+"F0.wireOp",EDGE,"E64"),sQuery(id+"F0.wireOp",EDGE,"E65"),sQuery(id+"F0.wireOp",EDGE,"E66"),sQuery(id+"F0.wireOp",EDGE,"E67"),sQuery(id+"F0.wireOp",EDGE,"E68"),sQuery(id+"F0.wireOp",EDGE,"E69"),sQuery(id+"F0.wireOp",EDGE,"E70"),sQuery(id+"F0.wireOp",EDGE,"E71"),sQuery(id+"F0.wireOp",EDGE,"E72"),sQuery(id+"F0.wireOp",EDGE,"E73"),sQuery(id+"F0.wireOp",EDGE,"E74"),sQuery(id+"F0.wireOp",EDGE,"E75"),sQuery(id+"F0.wireOp",EDGE,"E76"),sQuery(id+"F0.wireOp",EDGE,"E77"),sQuery(id+"F0.wireOp",EDGE,"E78"),sQuery(id+"F0.wireOp",EDGE,"E79"),sQuery(id+"F0.wireOp",EDGE,"E80"),sQuery(id+"F0.wireOp",EDGE,"E81"),sQuery(id+"F0.wireOp",EDGE,"E82"),sQuery(id+"F0.wireOp",EDGE,"E83"),sQuery(id+"F0.wireOp",EDGE,"E84"),sQuery(id+"F0.wireOp",EDGE,"E85"),sQuery(id+"F0.wireOp",EDGE,"E86"),sQuery(id+"F0.wireOp",EDGE,"E87"),sQuery(id+"F0.wireOp",EDGE,"E88"),sQuery(id+"F0.wireOp",EDGE,"E89"),sQuery(id+"F0.wireOp",EDGE,"E90"),sQuery(id+"F0.wireOp",EDGE,"E91"),sQuery(id+"F0.wireOp",EDGE,"E92"),sQuery(id+"F0.wireOp",EDGE,"E93"),sQuery(id+"F0.wireOp",EDGE,"E94"),sQuery(id+"F0.wireOp",EDGE,"E95"),sQuery(id+"F0.wireOp",EDGE,"E96"),sQuery(id+"F0.wireOp",EDGE,"E97"),sQuery(id+"F0.wireOp",EDGE,"E98"),sQuery(id+"F0.wireOp",EDGE,"E99"),sQuery(id+"F0.wireOp",EDGE,"E100"),sQuery(id+"F0.wireOp",EDGE,"E101"),sQuery(id+"F0.wireOp",EDGE,"E102"),sQuery(id+"F0.wireOp",EDGE,"E103"),sQuery(id+"F0.wireOp",EDGE,"E104"),sQuery(id+"F0.wireOp",EDGE,"E105"),sQuery(id+"F0.wireOp",EDGE,"E106"),sQuery(id+"F0.wireOp",EDGE,"E107"),sQuery(id+"F0.wireOp",EDGE,"E108"),sQuery(id+"F0.wireOp",EDGE,"E109"),sQuery(id+"F0.wireOp",EDGE,"E110"),sQuery(id+"F0.wireOp",EDGE,"E111"),sQuery(id+"F0.wireOp",EDGE,"E112"),sQuery(id+"F0.wireOp",EDGE,"E113"),sQuery(id+"F0.wireOp",EDGE,"E114"),sQuery(id+"F0.wireOp",EDGE,"E115"),sQuery(id+"F0.wireOp",EDGE,"E116"),sQuery(id+"F0.wireOp",EDGE,"E117"),sQuery(id+"F0.wireOp",EDGE,"E118"),sQuery(id+"F0.wireOp",EDGE,"E119"),sQuery(id+"F0.wireOp",EDGE,"E120"),sQuery(id+"F0.wireOp",EDGE,"E121"),sQuery(id+"F0.wireOp",EDGE,"E122"),sQuery(id+"F0.wireOp",EDGE,"E123"),sQuery(id+"F0.wireOp",EDGE,"E124"),sQuery(id+"F0.wireOp",EDGE,"E125"),sQuery(id+"F0.wireOp",EDGE,"E126"),sQuery(id+"F0.wireOp",EDGE,"E127"),sQuery(id+"F0.wireOp",EDGE,"E128"),sQuery(id+"F0.wireOp",EDGE,"E129"),sQuery(id+"F0.wireOp",EDGE,"E130"),sQuery(id+"F0.wireOp",EDGE,"E131"),sQuery(id+"F0.wireOp",EDGE,"E132"),sQuery(id+"F0.wireOp",EDGE,"E133"),sQuery(id+"F0.wireOp",EDGE,"E134"),sQuery(id+"F0.wireOp",EDGE,"E135"),sQuery(id+"F0.wireOp",EDGE,"E136"),sQuery(id+"F0.wireOp",EDGE,"E137"),sQuery(id+"F0.wireOp",EDGE,"E138"),sQuery(id+"F0.wireOp",EDGE,"E139"),sQuery(id+"F0.wireOp",EDGE,"E140"),sQuery(id+"F0.wireOp",EDGE,"E141"),sQuery(id+"F0.wireOp",EDGE,"E142"),sQuery(id+"F0.wireOp",EDGE,"E143"),sQuery(id+"F0.wireOp",EDGE,"E144"),sQuery(id+"F0.wireOp",EDGE,"E145"),sQuery(id+"F0.wireOp",EDGE,"E146"),sQuery(id+"F0.wireOp",EDGE,"E147"),sQuery(id+"F0.wireOp",EDGE,"E148"),sQuery(id+"F0.wireOp",EDGE,"E149"),sQuery(id+"F0.wireOp",EDGE,"E150"),sQuery(id+"F0.wireOp",EDGE,"E151"),sQuery(id+"F0.wireOp",EDGE,"E152"),sQuery(id+"F0.wireOp",EDGE,"E153"),sQuery(id+"F0.wireOp",EDGE,"E154"),sQuery(id+"F0.wireOp",EDGE,"E155"),sQuery(id+"F0.wireOp",EDGE,"E156"),sQuery(id+"F0.wireOp",EDGE,"E157"),sQuery(id+"F0.wireOp",EDGE,"E158"),sQuery(id+"F0.wireOp",EDGE,"E159"),sQuery(id+"F0.wireOp",EDGE,"E160"),sQuery(id+"F0.wireOp",EDGE,"E161"),sQuery(id+"F0.wireOp",EDGE,"E162"),sQuery(id+"F0.wireOp",EDGE,"E163"),sQuery(id+"F0.wireOp",EDGE,"E164"),sQuery(id+"F0.wireOp",EDGE,"E165"),sQuery(id+"F0.wireOp",EDGE,"E166"),sQuery(id+"F0.wireOp",EDGE,"E167"),sQuery(id+"F0.wireOp",EDGE,"E168"),sQuery(id+"F0.wireOp",EDGE,"E169"),sQuery(id+"F0.wireOp",EDGE,"E170"),sQuery(id+"F0.wireOp",EDGE,"E171"),sQuery(id+"F0.wireOp",EDGE,"E172"),sQuery(id+"F0.wireOp",EDGE,"E173"),sQuery(id+"F0.wireOp",EDGE,"E174"),sQuery(id+"F0.wireOp",EDGE,"E175"),sQuery(id+"F0.wireOp",EDGE,"E176"),sQuery(id+"F0.wireOp",EDGE,"E177"),sQuery(id+"F0.wireOp",EDGE,"E178"),sQuery(id+"F0.wireOp",EDGE,"E179"),sQuery(id+"F0.wireOp",EDGE,"E180"),sQuery(id+"F0.wireOp",EDGE,"E181"),sQuery(id+"F0.wireOp",EDGE,"E182"),sQuery(id+"F0.wireOp",EDGE,"E183"),sQuery(id+"F0.wireOp",EDGE,"E184"),sQuery(id+"F0.wireOp",EDGE,"E185"),sQuery(id+"F0.wireOp",EDGE,"E186"),sQuery(id+"F0.wireOp",EDGE,"E187"),sQuery(id+"F0.wireOp",EDGE,"E188"),sQuery(id+"F0.wireOp",EDGE,"E189"),sQuery(id+"F0.wireOp",EDGE,"E190"),sQuery(id+"F0.wireOp",EDGE,"E191"),sQuery(id+"F0.wireOp",EDGE,"E192"),sQuery(id+"F0.wireOp",EDGE,"E193"),sQuery(id+"F0.wireOp",EDGE,"E194"),sQuery(id+"F0.wireOp",EDGE,"E195"),sQuery(id+"F0.wireOp",EDGE,"E196"),sQuery(id+"F0.wireOp",EDGE,"E197"),sQuery(id+"F0.wireOp",EDGE,"E198"),sQuery(id+"F0.wireOp",EDGE,"E199"),sQuery(id+"F0.wireOp",EDGE,"E200"),sQuery(id+"F0.wireOp",EDGE,"E201"),sQuery(id+"F0.wireOp",EDGE,"E202"),sQuery(id+"F0.wireOp",EDGE,"E203"),sQuery(id+"F0.wireOp",EDGE,"E204"),sQuery(id+"F0.wireOp",EDGE,"E205"),sQuery(id+"F0.wireOp",EDGE,"E206"),sQuery(id+"F0.wireOp",EDGE,"E207"),sQuery(id+"F0.wireOp",EDGE,"E208"),sQuery(id+"F0.wireOp",EDGE,"E209"),sQuery(id+"F0.wireOp",EDGE,"E210"),sQuery(id+"F0.wireOp",EDGE,"E211"),sQuery(id+"F0.wireOp",EDGE,"E212"),sQuery(id+"F0.wireOp",EDGE,"E213"),sQuery(id+"F0.wireOp",EDGE,"E214"),sQuery(id+"F0.wireOp",EDGE,"E215"),sQuery(id+"F0.wireOp",EDGE,"E216"),sQuery(id+"F0.wireOp",EDGE,"E217"),sQuery(id+"F0.wireOp",EDGE,"E218"),sQuery(id+"F0.wireOp",EDGE,"E219"),sQuery(id+"F0.wireOp",EDGE,"E220"),sQuery(id+"F0.wireOp",EDGE,"E221"),sQuery(id+"F0.wireOp",EDGE,"E222"),sQuery(id+"F0.wireOp",EDGE,"E223"),sQuery(id+"F0.wireOp",EDGE,"E224"),sQuery(id+"F0.wireOp",EDGE,"E225"),sQuery(id+"F0.wireOp",EDGE,"E226"),sQuery(id+"F0.wireOp",EDGE,"E227"),sQuery(id+"F0.wireOp",EDGE,"E228"),sQuery(id+"F0.wireOp",EDGE,"E229"),sQuery(id+"F0.wireOp",EDGE,"E230"),sQuery(id+"F0.wireOp",EDGE,"E231"),sQuery(id+"F0.wireOp",EDGE,"E232"),sQuery(id+"F0.wireOp",EDGE,"E233"),sQuery(id+"F0.wireOp",EDGE,"E234"),sQuery(id+"F0.wireOp",EDGE,"E235"),sQuery(id+"F0.wireOp",EDGE,"E236"),sQuery(id+"F0.wireOp",EDGE,"E237"),sQuery(id+"F0.wireOp",EDGE,"E238"),sQuery(id+"F0.wireOp",EDGE,"E239"),sQuery(id+"F0.wireOp",EDGE,"E240"),sQuery(id+"F0.wireOp",EDGE,"E241"),sQuery(id+"F0.wireOp",EDGE,"E242"),sQuery(id+"F0.wireOp",EDGE,"E243"),sQuery(id+"F0.wireOp",EDGE,"E244"),sQuery(id+"F0.wireOp",EDGE,"E245"),sQuery(id+"F0.wireOp",EDGE,"E246"),sQuery(id+"F0.wireOp",EDGE,"E247"),sQuery(id+"F0.wireOp",EDGE,"E248"),sQuery(id+"F0.wireOp",EDGE,"E249"),sQuery(id+"F0.wireOp",EDGE,"E250"),sQuery(id+"F0.wireOp",EDGE,"E251"),sQuery(id+"F0.wireOp",EDGE,"E252"),sQuery(id+"F0.wireOp",EDGE,"E253"),sQuery(id+"F0.wireOp",EDGE,"E254"),sQuery(id+"F0.wireOp",EDGE,"E255"),sQuery(id+"F0.wireOp",EDGE,"E256"),sQuery(id+"F0.wireOp",EDGE,"E257"),sQuery(id+"F0.wireOp",EDGE,"E258"),sQuery(id+"F0.wireOp",EDGE,"E259"),sQuery(id+"F0.wireOp",EDGE,"E260"),sQuery(id+"F0.wireOp",EDGE,"E261"),sQuery(id+"F0.wireOp",EDGE,"E262"),sQuery(id+"F0.wireOp",EDGE,"E263"),sQuery(id+"F0.wireOp",EDGE,"E264"),sQuery(id+"F0.wireOp",EDGE,"E265"),sQuery(id+"F0.wireOp",EDGE,"E266"),sQuery(id+"F0.wireOp",EDGE,"E267"),sQuery(id+"F0.wireOp",EDGE,"E268"),sQuery(id+"F0.wireOp",EDGE,"E269"),sQuery(id+"F0.wireOp",EDGE,"E270"),sQuery(id+"F0.wireOp",EDGE,"E271"),sQuery(id+"F0.wireOp",EDGE,"E272"),sQuery(id+"F0.wireOp",EDGE,"E273"),sQuery(id+"F0.wireOp",EDGE,"E274"),sQuery(id+"F0.wireOp",EDGE,"E275"),sQuery(id+"F0.wireOp",EDGE,"E276"),sQuery(id+"F0.wireOp",EDGE,"E277"),sQuery(id+"F0.wireOp",EDGE,"E278"),sQuery(id+"F0.wireOp",EDGE,"E279"),sQuery(id+"F0.wireOp",EDGE,"E280"),sQuery(id+"F0.wireOp",EDGE,"E281"),sQuery(id+"F0.wireOp",EDGE,"E282"),sQuery(id+"F0.wireOp",EDGE,"E283"),sQuery(id+"F0.wireOp",EDGE,"E284"),sQuery(id+"F0.wireOp",EDGE,"E285"),sQuery(id+"F0.wireOp",EDGE,"E286"),sQuery(id+"F0.wireOp",EDGE,"E287"),sQuery(id+"F0.wireOp",EDGE,"E288"),sQuery(id+"F0.wireOp",EDGE,"E289"),sQuery(id+"F0.wireOp",EDGE,"E290"),sQuery(id+"F0.wireOp",EDGE,"E291"),sQuery(id+"F0.wireOp",EDGE,"E292"),sQuery(id+"F0.wireOp",EDGE,"E293"),sQuery(id+"F0.wireOp",EDGE,"E294"),sQuery(id+"F0.wireOp",EDGE,"E295"),sQuery(id+"F0.wireOp",EDGE,"E296"),sQuery(id+"F0.wireOp",EDGE,"E297"),sQuery(id+"F0.wireOp",EDGE,"E298"),sQuery(id+"F0.wireOp",EDGE,"E299"),sQuery(id+"F0.wireOp",EDGE,"E300"),sQuery(id+"F0.wireOp",EDGE,"E301"),sQuery(id+"F0.wireOp",EDGE,"E302"),sQuery(id+"F0.wireOp",EDGE,"E303"),sQuery(id+"F0.wireOp",EDGE,"E304"),sQuery(id+"F0.wireOp",EDGE,"E305"),sQuery(id+"F0.wireOp",EDGE,"E306"),sQuery(id+"F0.wireOp",EDGE,"E307"),sQuery(id+"F0.wireOp",EDGE,"E308"),sQuery(id+"F0.wireOp",EDGE,"E309"),sQuery(id+"F0.wireOp",EDGE,"E310"),sQuery(id+"F0.wireOp",EDGE,"E311"),sQuery(id+"F0.wireOp",EDGE,"E312"),sQuery(id+"F0.wireOp",EDGE,"E313"),sQuery(id+"F0.wireOp",EDGE,"E314"),sQuery(id+"F0.wireOp",EDGE,"E315"),sQuery(id+"F0.wireOp",EDGE,"E316"),sQuery(id+"F0.wireOp",EDGE,"E317"),sQuery(id+"F0.wireOp",EDGE,"E318"),sQuery(id+"F0.wireOp",EDGE,"E319"),sQuery(id+"F0.wireOp",EDGE,"E320"),sQuery(id+"F0.wireOp",EDGE,"E321")])]});
            var Q1;
            Q1=qCreatedBy(makeId("Origin.pointOp"),VERTEX);
            transform(context, id + "F2", {"entities" : qUnion([Q0]), "transformType" : TransformType.SCALE_UNIFORMLY, "scale" : 6, "scalePoint" : qUnion([Q1]), "makeCopy" : false});
        }
        {
            var Q0;
            Q0=makeQuery(id+"F1.opExtrude","CAP_FACE",FACE,{"disambiguationData":[OSD([sQuery(id+"F0.wireOp",EDGE,"E0"),sQuery(id+"F0.wireOp",EDGE,"E1"),sQuery(id+"F0.wireOp",EDGE,"E2"),sQuery(id+"F0.wireOp",EDGE,"E3"),sQuery(id+"F0.wireOp",EDGE,"E4"),sQuery(id+"F0.wireOp",EDGE,"E5"),sQuery(id+"F0.wireOp",EDGE,"E6"),sQuery(id+"F0.wireOp",EDGE,"E7"),sQuery(id+"F0.wireOp",EDGE,"E8"),sQuery(id+"F0.wireOp",EDGE,"E9"),sQuery(id+"F0.wireOp",EDGE,"E10"),sQuery(id+"F0.wireOp",EDGE,"E11"),sQuery(id+"F0.wireOp",EDGE,"E12"),sQuery(id+"F0.wireOp",EDGE,"E13"),sQuery(id+"F0.wireOp",EDGE,"E14"),sQuery(id+"F0.wireOp",EDGE,"E15"),sQuery(id+"F0.wireOp",EDGE,"E16"),sQuery(id+"F0.wireOp",EDGE,"E17"),sQuery(id+"F0.wireOp",EDGE,"E18"),sQuery(id+"F0.wireOp",EDGE,"E19"),sQuery(id+"F0.wireOp",EDGE,"E20"),sQuery(id+"F0.wireOp",EDGE,"E21"),sQuery(id+"F0.wireOp",EDGE,"E22"),sQuery(id+"F0.wireOp",EDGE,"E23"),sQuery(id+"F0.wireOp",EDGE,"E24"),sQuery(id+"F0.wireOp",EDGE,"E25"),sQuery(id+"F0.wireOp",EDGE,"E26"),sQuery(id+"F0.wireOp",EDGE,"E27"),sQuery(id+"F0.wireOp",EDGE,"E28"),sQuery(id+"F0.wireOp",EDGE,"E29"),sQuery(id+"F0.wireOp",EDGE,"E30"),sQuery(id+"F0.wireOp",EDGE,"E31"),sQuery(id+"F0.wireOp",EDGE,"E32"),sQuery(id+"F0.wireOp",EDGE,"E33"),sQuery(id+"F0.wireOp",EDGE,"E34"),sQuery(id+"F0.wireOp",EDGE,"E35"),sQuery(id+"F0.wireOp",EDGE,"E36"),sQuery(id+"F0.wireOp",EDGE,"E37"),sQuery(id+"F0.wireOp",EDGE,"E38"),sQuery(id+"F0.wireOp",EDGE,"E39"),sQuery(id+"F0.wireOp",EDGE,"E40"),sQuery(id+"F0.wireOp",EDGE,"E41"),sQuery(id+"F0.wireOp",EDGE,"E42"),sQuery(id+"F0.wireOp",EDGE,"E43"),sQuery(id+"F0.wireOp",EDGE,"E44"),sQuery(id+"F0.wireOp",EDGE,"E45"),sQuery(id+"F0.wireOp",EDGE,"E46"),sQuery(id+"F0.wireOp",EDGE,"E47"),sQuery(id+"F0.wireOp",EDGE,"E48"),sQuery(id+"F0.wireOp",EDGE,"E49"),sQuery(id+"F0.wireOp",EDGE,"E50"),sQuery(id+"F0.wireOp",EDGE,"E51"),sQuery(id+"F0.wireOp",EDGE,"E52"),sQuery(id+"F0.wireOp",EDGE,"E53"),sQuery(id+"F0.wireOp",EDGE,"E54"),sQuery(id+"F0.wireOp",EDGE,"E55"),sQuery(id+"F0.wireOp",EDGE,"E56"),sQuery(id+"F0.wireOp",EDGE,"E57"),sQuery(id+"F0.wireOp",EDGE,"E58"),sQuery(id+"F0.wireOp",EDGE,"E59"),sQuery(id+"F0.wireOp",EDGE,"E60"),sQuery(id+"F0.wireOp",EDGE,"E61"),sQuery(id+"F0.wireOp",EDGE,"E62"),sQuery(id+"F0.wireOp",EDGE,"E63"),sQuery(id+"F0.wireOp",EDGE,"E64"),sQuery(id+"F0.wireOp",EDGE,"E65"),sQuery(id+"F0.wireOp",EDGE,"E66"),sQuery(id+"F0.wireOp",EDGE,"E67"),sQuery(id+"F0.wireOp",EDGE,"E68"),sQuery(id+"F0.wireOp",EDGE,"E69"),sQuery(id+"F0.wireOp",EDGE,"E70"),sQuery(id+"F0.wireOp",EDGE,"E71"),sQuery(id+"F0.wireOp",EDGE,"E72"),sQuery(id+"F0.wireOp",EDGE,"E73"),sQuery(id+"F0.wireOp",EDGE,"E74"),sQuery(id+"F0.wireOp",EDGE,"E75"),sQuery(id+"F0.wireOp",EDGE,"E76"),sQuery(id+"F0.wireOp",EDGE,"E77"),sQuery(id+"F0.wireOp",EDGE,"E78"),sQuery(id+"F0.wireOp",EDGE,"E79"),sQuery(id+"F0.wireOp",EDGE,"E80"),sQuery(id+"F0.wireOp",EDGE,"E81"),sQuery(id+"F0.wireOp",EDGE,"E82"),sQuery(id+"F0.wireOp",EDGE,"E83"),sQuery(id+"F0.wireOp",EDGE,"E84"),sQuery(id+"F0.wireOp",EDGE,"E85"),sQuery(id+"F0.wireOp",EDGE,"E86"),sQuery(id+"F0.wireOp",EDGE,"E87"),sQuery(id+"F0.wireOp",EDGE,"E88"),sQuery(id+"F0.wireOp",EDGE,"E89"),sQuery(id+"F0.wireOp",EDGE,"E90"),sQuery(id+"F0.wireOp",EDGE,"E91"),sQuery(id+"F0.wireOp",EDGE,"E92"),sQuery(id+"F0.wireOp",EDGE,"E93"),sQuery(id+"F0.wireOp",EDGE,"E94"),sQuery(id+"F0.wireOp",EDGE,"E95"),sQuery(id+"F0.wireOp",EDGE,"E96"),sQuery(id+"F0.wireOp",EDGE,"E97"),sQuery(id+"F0.wireOp",EDGE,"E98"),sQuery(id+"F0.wireOp",EDGE,"E99"),sQuery(id+"F0.wireOp",EDGE,"E100"),sQuery(id+"F0.wireOp",EDGE,"E101"),sQuery(id+"F0.wireOp",EDGE,"E102"),sQuery(id+"F0.wireOp",EDGE,"E103"),sQuery(id+"F0.wireOp",EDGE,"E104"),sQuery(id+"F0.wireOp",EDGE,"E105"),sQuery(id+"F0.wireOp",EDGE,"E106"),sQuery(id+"F0.wireOp",EDGE,"E107"),sQuery(id+"F0.wireOp",EDGE,"E108"),sQuery(id+"F0.wireOp",EDGE,"E109"),sQuery(id+"F0.wireOp",EDGE,"E110"),sQuery(id+"F0.wireOp",EDGE,"E111"),sQuery(id+"F0.wireOp",EDGE,"E112"),sQuery(id+"F0.wireOp",EDGE,"E113"),sQuery(id+"F0.wireOp",EDGE,"E114"),sQuery(id+"F0.wireOp",EDGE,"E115"),sQuery(id+"F0.wireOp",EDGE,"E116"),sQuery(id+"F0.wireOp",EDGE,"E117"),sQuery(id+"F0.wireOp",EDGE,"E118"),sQuery(id+"F0.wireOp",EDGE,"E119"),sQuery(id+"F0.wireOp",EDGE,"E120"),sQuery(id+"F0.wireOp",EDGE,"E121"),sQuery(id+"F0.wireOp",EDGE,"E122"),sQuery(id+"F0.wireOp",EDGE,"E123"),sQuery(id+"F0.wireOp",EDGE,"E124"),sQuery(id+"F0.wireOp",EDGE,"E125"),sQuery(id+"F0.wireOp",EDGE,"E126"),sQuery(id+"F0.wireOp",EDGE,"E127"),sQuery(id+"F0.wireOp",EDGE,"E128"),sQuery(id+"F0.wireOp",EDGE,"E129"),sQuery(id+"F0.wireOp",EDGE,"E130"),sQuery(id+"F0.wireOp",EDGE,"E131"),sQuery(id+"F0.wireOp",EDGE,"E132"),sQuery(id+"F0.wireOp",EDGE,"E133"),sQuery(id+"F0.wireOp",EDGE,"E134"),sQuery(id+"F0.wireOp",EDGE,"E135"),sQuery(id+"F0.wireOp",EDGE,"E136"),sQuery(id+"F0.wireOp",EDGE,"E137"),sQuery(id+"F0.wireOp",EDGE,"E138"),sQuery(id+"F0.wireOp",EDGE,"E139"),sQuery(id+"F0.wireOp",EDGE,"E140"),sQuery(id+"F0.wireOp",EDGE,"E141"),sQuery(id+"F0.wireOp",EDGE,"E142"),sQuery(id+"F0.wireOp",EDGE,"E143"),sQuery(id+"F0.wireOp",EDGE,"E144"),sQuery(id+"F0.wireOp",EDGE,"E145"),sQuery(id+"F0.wireOp",EDGE,"E146"),sQuery(id+"F0.wireOp",EDGE,"E147"),sQuery(id+"F0.wireOp",EDGE,"E148"),sQuery(id+"F0.wireOp",EDGE,"E149"),sQuery(id+"F0.wireOp",EDGE,"E150"),sQuery(id+"F0.wireOp",EDGE,"E151"),sQuery(id+"F0.wireOp",EDGE,"E152"),sQuery(id+"F0.wireOp",EDGE,"E153"),sQuery(id+"F0.wireOp",EDGE,"E154"),sQuery(id+"F0.wireOp",EDGE,"E155"),sQuery(id+"F0.wireOp",EDGE,"E156"),sQuery(id+"F0.wireOp",EDGE,"E157"),sQuery(id+"F0.wireOp",EDGE,"E158"),sQuery(id+"F0.wireOp",EDGE,"E159"),sQuery(id+"F0.wireOp",EDGE,"E160"),sQuery(id+"F0.wireOp",EDGE,"E161"),sQuery(id+"F0.wireOp",EDGE,"E162"),sQuery(id+"F0.wireOp",EDGE,"E163"),sQuery(id+"F0.wireOp",EDGE,"E164"),sQuery(id+"F0.wireOp",EDGE,"E165"),sQuery(id+"F0.wireOp",EDGE,"E166"),sQuery(id+"F0.wireOp",EDGE,"E167"),sQuery(id+"F0.wireOp",EDGE,"E168"),sQuery(id+"F0.wireOp",EDGE,"E169"),sQuery(id+"F0.wireOp",EDGE,"E170"),sQuery(id+"F0.wireOp",EDGE,"E171"),sQuery(id+"F0.wireOp",EDGE,"E172"),sQuery(id+"F0.wireOp",EDGE,"E173"),sQuery(id+"F0.wireOp",EDGE,"E174"),sQuery(id+"F0.wireOp",EDGE,"E175"),sQuery(id+"F0.wireOp",EDGE,"E176"),sQuery(id+"F0.wireOp",EDGE,"E177"),sQuery(id+"F0.wireOp",EDGE,"E178"),sQuery(id+"F0.wireOp",EDGE,"E179"),sQuery(id+"F0.wireOp",EDGE,"E180"),sQuery(id+"F0.wireOp",EDGE,"E181"),sQuery(id+"F0.wireOp",EDGE,"E182"),sQuery(id+"F0.wireOp",EDGE,"E183"),sQuery(id+"F0.wireOp",EDGE,"E184"),sQuery(id+"F0.wireOp",EDGE,"E185"),sQuery(id+"F0.wireOp",EDGE,"E186"),sQuery(id+"F0.wireOp",EDGE,"E187"),sQuery(id+"F0.wireOp",EDGE,"E188"),sQuery(id+"F0.wireOp",EDGE,"E189"),sQuery(id+"F0.wireOp",EDGE,"E190"),sQuery(id+"F0.wireOp",EDGE,"E191"),sQuery(id+"F0.wireOp",EDGE,"E192"),sQuery(id+"F0.wireOp",EDGE,"E193"),sQuery(id+"F0.wireOp",EDGE,"E194"),sQuery(id+"F0.wireOp",EDGE,"E195"),sQuery(id+"F0.wireOp",EDGE,"E196"),sQuery(id+"F0.wireOp",EDGE,"E197"),sQuery(id+"F0.wireOp",EDGE,"E198"),sQuery(id+"F0.wireOp",EDGE,"E199"),sQuery(id+"F0.wireOp",EDGE,"E200"),sQuery(id+"F0.wireOp",EDGE,"E201"),sQuery(id+"F0.wireOp",EDGE,"E202"),sQuery(id+"F0.wireOp",EDGE,"E203"),sQuery(id+"F0.wireOp",EDGE,"E204"),sQuery(id+"F0.wireOp",EDGE,"E205"),sQuery(id+"F0.wireOp",EDGE,"E206"),sQuery(id+"F0.wireOp",EDGE,"E207"),sQuery(id+"F0.wireOp",EDGE,"E208"),sQuery(id+"F0.wireOp",EDGE,"E209"),sQuery(id+"F0.wireOp",EDGE,"E210"),sQuery(id+"F0.wireOp",EDGE,"E211"),sQuery(id+"F0.wireOp",EDGE,"E212"),sQuery(id+"F0.wireOp",EDGE,"E213"),sQuery(id+"F0.wireOp",EDGE,"E214"),sQuery(id+"F0.wireOp",EDGE,"E215"),sQuery(id+"F0.wireOp",EDGE,"E216"),sQuery(id+"F0.wireOp",EDGE,"E217"),sQuery(id+"F0.wireOp",EDGE,"E218"),sQuery(id+"F0.wireOp",EDGE,"E219"),sQuery(id+"F0.wireOp",EDGE,"E220"),sQuery(id+"F0.wireOp",EDGE,"E221"),sQuery(id+"F0.wireOp",EDGE,"E222"),sQuery(id+"F0.wireOp",EDGE,"E223"),sQuery(id+"F0.wireOp",EDGE,"E224"),sQuery(id+"F0.wireOp",EDGE,"E225"),sQuery(id+"F0.wireOp",EDGE,"E226"),sQuery(id+"F0.wireOp",EDGE,"E227"),sQuery(id+"F0.wireOp",EDGE,"E228"),sQuery(id+"F0.wireOp",EDGE,"E229"),sQuery(id+"F0.wireOp",EDGE,"E230"),sQuery(id+"F0.wireOp",EDGE,"E231"),sQuery(id+"F0.wireOp",EDGE,"E232"),sQuery(id+"F0.wireOp",EDGE,"E233"),sQuery(id+"F0.wireOp",EDGE,"E234"),sQuery(id+"F0.wireOp",EDGE,"E235"),sQuery(id+"F0.wireOp",EDGE,"E236"),sQuery(id+"F0.wireOp",EDGE,"E237"),sQuery(id+"F0.wireOp",EDGE,"E238"),sQuery(id+"F0.wireOp",EDGE,"E239"),sQuery(id+"F0.wireOp",EDGE,"E240"),sQuery(id+"F0.wireOp",EDGE,"E241"),sQuery(id+"F0.wireOp",EDGE,"E242"),sQuery(id+"F0.wireOp",EDGE,"E243"),sQuery(id+"F0.wireOp",EDGE,"E244"),sQuery(id+"F0.wireOp",EDGE,"E245"),sQuery(id+"F0.wireOp",EDGE,"E246"),sQuery(id+"F0.wireOp",EDGE,"E247"),sQuery(id+"F0.wireOp",EDGE,"E248"),sQuery(id+"F0.wireOp",EDGE,"E249"),sQuery(id+"F0.wireOp",EDGE,"E250"),sQuery(id+"F0.wireOp",EDGE,"E251"),sQuery(id+"F0.wireOp",EDGE,"E252"),sQuery(id+"F0.wireOp",EDGE,"E253"),sQuery(id+"F0.wireOp",EDGE,"E254"),sQuery(id+"F0.wireOp",EDGE,"E255"),sQuery(id+"F0.wireOp",EDGE,"E256"),sQuery(id+"F0.wireOp",EDGE,"E257"),sQuery(id+"F0.wireOp",EDGE,"E258"),sQuery(id+"F0.wireOp",EDGE,"E259"),sQuery(id+"F0.wireOp",EDGE,"E260"),sQuery(id+"F0.wireOp",EDGE,"E261"),sQuery(id+"F0.wireOp",EDGE,"E262"),sQuery(id+"F0.wireOp",EDGE,"E263"),sQuery(id+"F0.wireOp",EDGE,"E264"),sQuery(id+"F0.wireOp",EDGE,"E265"),sQuery(id+"F0.wireOp",EDGE,"E266"),sQuery(id+"F0.wireOp",EDGE,"E267"),sQuery(id+"F0.wireOp",EDGE,"E268"),sQuery(id+"F0.wireOp",EDGE,"E269"),sQuery(id+"F0.wireOp",EDGE,"E270"),sQuery(id+"F0.wireOp",EDGE,"E271"),sQuery(id+"F0.wireOp",EDGE,"E272"),sQuery(id+"F0.wireOp",EDGE,"E273"),sQuery(id+"F0.wireOp",EDGE,"E274"),sQuery(id+"F0.wireOp",EDGE,"E275"),sQuery(id+"F0.wireOp",EDGE,"E276"),sQuery(id+"F0.wireOp",EDGE,"E277"),sQuery(id+"F0.wireOp",EDGE,"E278"),sQuery(id+"F0.wireOp",EDGE,"E279"),sQuery(id+"F0.wireOp",EDGE,"E280"),sQuery(id+"F0.wireOp",EDGE,"E281"),sQuery(id+"F0.wireOp",EDGE,"E282"),sQuery(id+"F0.wireOp",EDGE,"E283"),sQuery(id+"F0.wireOp",EDGE,"E284"),sQuery(id+"F0.wireOp",EDGE,"E285"),sQuery(id+"F0.wireOp",EDGE,"E286"),sQuery(id+"F0.wireOp",EDGE,"E287"),sQuery(id+"F0.wireOp",EDGE,"E288"),sQuery(id+"F0.wireOp",EDGE,"E289"),sQuery(id+"F0.wireOp",EDGE,"E290"),sQuery(id+"F0.wireOp",EDGE,"E291"),sQuery(id+"F0.wireOp",EDGE,"E292"),sQuery(id+"F0.wireOp",EDGE,"E293"),sQuery(id+"F0.wireOp",EDGE,"E294"),sQuery(id+"F0.wireOp",EDGE,"E295"),sQuery(id+"F0.wireOp",EDGE,"E296"),sQuery(id+"F0.wireOp",EDGE,"E297"),sQuery(id+"F0.wireOp",EDGE,"E298"),sQuery(id+"F0.wireOp",EDGE,"E299"),sQuery(id+"F0.wireOp",EDGE,"E300"),sQuery(id+"F0.wireOp",EDGE,"E301"),sQuery(id+"F0.wireOp",EDGE,"E302"),sQuery(id+"F0.wireOp",EDGE,"E303"),sQuery(id+"F0.wireOp",EDGE,"E304"),sQuery(id+"F0.wireOp",EDGE,"E305"),sQuery(id+"F0.wireOp",EDGE,"E306"),sQuery(id+"F0.wireOp",EDGE,"E307"),sQuery(id+"F0.wireOp",EDGE,"E308"),sQuery(id+"F0.wireOp",EDGE,"E309"),sQuery(id+"F0.wireOp",EDGE,"E310"),sQuery(id+"F0.wireOp",EDGE,"E311"),sQuery(id+"F0.wireOp",EDGE,"E312"),sQuery(id+"F0.wireOp",EDGE,"E313"),sQuery(id+"F0.wireOp",EDGE,"E314"),sQuery(id+"F0.wireOp",EDGE,"E315"),sQuery(id+"F0.wireOp",EDGE,"E316"),sQuery(id+"F0.wireOp",EDGE,"E317"),sQuery(id+"F0.wireOp",EDGE,"E318"),sQuery(id+"F0.wireOp",EDGE,"E319"),sQuery(id+"F0.wireOp",EDGE,"E320"),sQuery(id+"F0.wireOp",EDGE,"E321")])],"isStart":false});
            extrude(context, id + "F3", {"entities" : qUnion([Q0]), "operationType" : NewBodyOperationType.ADD, "depth" : 1.5 * mm, "offsetDistance" : 25 * mm});
        }
    });
